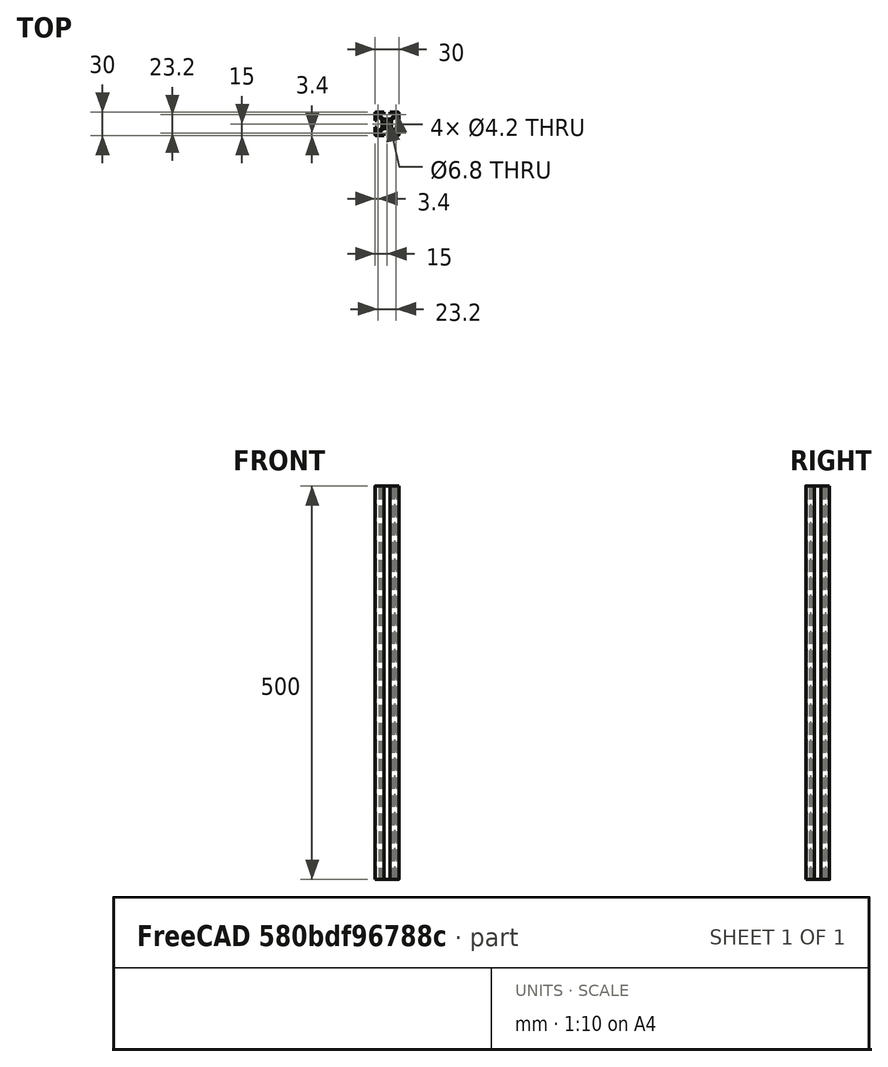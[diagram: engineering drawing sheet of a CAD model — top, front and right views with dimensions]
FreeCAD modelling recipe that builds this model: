
FCSTD DOCUMENT  (FreeCAD 0.19R24267 +99 (Git))
Label: misumi_profile_hfs_serie6_w8_30x30_Parametrique
License: All rights reserved
LicenseURL: http://en.wikipedia.org/wiki/All_rights_reserved
objects: Sketcher::SketchObject×1, Spreadsheet::Sheet×1, PartDesign::Pad×1, PartDesign::Body×1, App::Part×1
note: 4 computed .brp shape members not serialized (recipe doc carries the construction recipe); baked Part::Feature solids carry a one-line shape summary decoded from their .brp

FEATURE [Sketcher::SketchObject] Sketch  label="Profile"
  FullyConstrained = true
  MapMode = 5
  sketch-geometry (53):
    g0: LineSegment StartX=-6 StartY=-4.58579 StartZ=0 EndX=-6 EndY=4.58579 EndZ=0
    g1: LineSegment StartX=4.58579 StartY=6 StartZ=0 EndX=-4.58579 EndY=6 EndZ=0
    g2: LineSegment StartX=-6 StartY=4.58579 StartZ=0 EndX=-9.66421 EndY=8.25 EndZ=0
    g3: LineSegment StartX=-4.58579 StartY=6 StartZ=0 EndX=-8.25 EndY=9.66421 EndZ=0
    g4: LineSegment StartX=-9.66421 StartY=8.25 StartZ=0 EndX=-13 EndY=8.25 EndZ=0
    g5: LineSegment StartX=-13 StartY=8.25 StartZ=0 EndX=-13 EndY=4 EndZ=0
    g6: LineSegment StartX=-8.25 StartY=9.66421 StartZ=0 EndX=-8.25 EndY=13 EndZ=0
    g7: LineSegment StartX=-8.25 StartY=13 StartZ=0 EndX=-4 EndY=13 EndZ=0
    g8: LineSegment StartX=-13 StartY=4 StartZ=0 EndX=-15 EndY=4 EndZ=0
    g9: LineSegment StartX=-4 StartY=13 StartZ=0 EndX=-4 EndY=15 EndZ=0
    g10: LineSegment StartX=-4 StartY=15 StartZ=0 EndX=-14 EndY=15 EndZ=0
    g11: LineSegment StartX=-15 StartY=4 StartZ=0 EndX=-15 EndY=14 EndZ=0
    g12: ArcOfCircle CenterX=-14 CenterY=14 CenterZ=0 NormalX=0 NormalY=0 NormalZ=1 AngleXU=0 Radius=1 StartAngle=1.5708 EndAngle=3.14159
    g13: Circle CenterX=-11.6 CenterY=11.6 CenterZ=0 NormalX=0 NormalY=0 NormalZ=1 AngleXU=0 Radius=2.1
    g14: Circle CenterX=0 CenterY=0 CenterZ=0 NormalX=0 NormalY=0 NormalZ=1 AngleXU=0 Radius=3.4
    g15: LineSegment StartX=6 StartY=4.58579 StartZ=0 EndX=6 EndY=-4.58579 EndZ=0
    g16: LineSegment StartX=4.58579 StartY=6 StartZ=0 EndX=8.25 EndY=9.66421 EndZ=0
    g17: LineSegment StartX=8.25 StartY=9.66421 StartZ=0 EndX=8.25 EndY=13 EndZ=0
    g18: LineSegment StartX=8.25 StartY=13 StartZ=0 EndX=4 EndY=13 EndZ=0
    g19: LineSegment StartX=4 StartY=13 StartZ=0 EndX=4 EndY=15 EndZ=0
    g20: LineSegment StartX=6 StartY=4.58579 StartZ=0 EndX=9.66421 EndY=8.25 EndZ=0
    g21: LineSegment StartX=9.66421 StartY=8.25 StartZ=0 EndX=13 EndY=8.25 EndZ=0
    g22: LineSegment StartX=13 StartY=8.25 StartZ=0 EndX=13 EndY=4 EndZ=0
    g23: LineSegment StartX=13 StartY=4 StartZ=0 EndX=15 EndY=4 EndZ=0
    g24: LineSegment StartX=15 StartY=4 StartZ=0 EndX=15 EndY=14 EndZ=0
    g25: Circle CenterX=11.6 CenterY=11.6 CenterZ=0 NormalX=0 NormalY=0 NormalZ=1 AngleXU=0 Radius=2.1
    g26: LineSegment StartX=4 StartY=15 StartZ=0 EndX=14 EndY=15 EndZ=0
    g27: ArcOfCircle CenterX=14 CenterY=14 CenterZ=0 NormalX=0 NormalY=0 NormalZ=1 AngleXU=0 Radius=1 StartAngle=6.28319 EndAngle=7.85398
    g28: LineSegment StartX=6 StartY=-4.58579 StartZ=0 EndX=9.66421 EndY=-8.25 EndZ=0
    g29: LineSegment StartX=9.66421 StartY=-8.25 StartZ=0 EndX=13 EndY=-8.25 EndZ=0
    g30: LineSegment StartX=13 StartY=-8.25 StartZ=0 EndX=13 EndY=-4 EndZ=0
    g31: LineSegment StartX=13 StartY=-4 StartZ=0 EndX=15 EndY=-4 EndZ=0
    g32: LineSegment StartX=15 StartY=-4 StartZ=0 EndX=15 EndY=-14 EndZ=0
    g33: LineSegment StartX=14 StartY=-15 StartZ=0 EndX=4 EndY=-15 EndZ=0
    g34: LineSegment StartX=4 StartY=-15 StartZ=0 EndX=4 EndY=-13 EndZ=0
    g35: LineSegment StartX=4 StartY=-13 StartZ=0 EndX=8.25 EndY=-13 EndZ=0
    g36: LineSegment StartX=8.25 StartY=-13 StartZ=0 EndX=8.25 EndY=-9.66421 EndZ=0
    g37: LineSegment StartX=8.25 StartY=-9.66421 StartZ=0 EndX=4.58579 EndY=-6 EndZ=0
    g38: LineSegment StartX=4.58579 StartY=-6 StartZ=0 EndX=-4.58579 EndY=-6 EndZ=0
    g39: LineSegment StartX=-4.58579 StartY=-6 StartZ=0 EndX=-8.25 EndY=-9.66421 EndZ=0
    g40: LineSegment StartX=-8.25 StartY=-9.66421 StartZ=0 EndX=-8.25 EndY=-13 EndZ=0
    g41: LineSegment StartX=-8.25 StartY=-13 StartZ=0 EndX=-4 EndY=-13 EndZ=0
    g42: LineSegment StartX=-4 StartY=-13 StartZ=0 EndX=-4 EndY=-15 EndZ=0
    g43: LineSegment StartX=-4 StartY=-15 StartZ=0 EndX=-14 EndY=-15 EndZ=0
    g44: ArcOfCircle CenterX=14 CenterY=-14 CenterZ=0 NormalX=0 NormalY=0 NormalZ=1 AngleXU=0 Radius=1 StartAngle=4.71239 EndAngle=6.28319
    g45: LineSegment StartX=-6 StartY=-4.58579 StartZ=0 EndX=-9.66421 EndY=-8.25 EndZ=0
    g46: LineSegment StartX=-9.66421 StartY=-8.25 StartZ=0 EndX=-13 EndY=-8.25 EndZ=0
    g47: LineSegment StartX=-13 StartY=-8.25 StartZ=0 EndX=-13 EndY=-4 EndZ=0
    g48: LineSegment StartX=-13 StartY=-4 StartZ=0 EndX=-15 EndY=-4 EndZ=0
    g49: LineSegment StartX=-15 StartY=-4 StartZ=0 EndX=-15 EndY=-14 EndZ=0
    g50: ArcOfCircle CenterX=-14 CenterY=-14 CenterZ=0 NormalX=0 NormalY=0 NormalZ=1 AngleXU=0 Radius=1 StartAngle=3.14159 EndAngle=4.71239
    g51: Circle CenterX=-11.6 CenterY=-11.6 CenterZ=0 NormalX=0 NormalY=0 NormalZ=1 AngleXU=0 Radius=2.1
    g52: Circle CenterX=11.6 CenterY=-11.6 CenterZ=0 NormalX=0 NormalY=0 NormalZ=1 AngleXU=0 Radius=2.1
  constraints (124):
    c: DistanceX(g-1,g0) = -6
    c: Vertical(g0)
    c: Equal(g0,g1)
    c: Coincident(g0,g2)
    c: Angle(g2,g0) = 2.35619
    c: Coincident(g3,g1)
    c: Parallel(g2,g3)
    c: Equal(g3,g2)
    c: Coincident(g4,g2)
    c: Horizontal(g4)
    c: Coincident(g4,g5)
    c: Vertical(g5)
    c: Coincident(g6,g3)
    c: Vertical(g6)
    c: Equal(g4,g6)
    c: Coincident(g7,g6)
    c: Horizontal(g7)
    c: Equal(g7,g5)
    c: Coincident(g8,g5)
    c: Horizontal(g8)
    c: Coincident(g9,g7)
    c: Vertical(g9)
    c: DistanceX(g-1,g7) = -4
    c: DistanceY(g9) = 2
    c: Coincident(g10,g9)
    c: Horizontal(g10)
    c: Coincident(g11,g8)
    c: Vertical(g11)
    c: Equal(g10,g11)
    c: DistanceY(g-1,g10) = 15
    c: Coincident(g12,g10)
    c: Coincident(g12,g11)
    c: Radius(g12) = 1
    c: Tangent(g12,g11)
    c: Equal(g8,g9)
    c: Distance(g1,g0) = 2
    c: DistanceX(g-1,g3) = -8.25
    c: Radius(g13) = 2.1
    c: DistanceY(g-1,g13) = 11.6
    c: DistanceX(g-1,g13) = -11.6
    c: Coincident(g14,g-1)
    c: Radius(g14) = 3.4
    c: DistanceY(g-1,g1) = 6
    c: DistanceY(g-1,g5) = 4
    c: Symmetric(g15,g0,g-2)
    c: Symmetric(g0,g15,g-2)
    c: Coincident(g16,g1)
    c: Symmetric(g1,g1,g-2)
    c: Symmetric(g16,g3,g-2)
    c: Coincident(g17,g16)
    c: Symmetric(g17,g6,g-2)
    c: Coincident(g18,g17)
    c: Symmetric(g18,g7,g-2)
    c: Coincident(g19,g18)
    c: Symmetric(g19,g9,g-2)
    c: Coincident(g20,g21)
    c: Coincident(g21,g22)
    c: Coincident(g22,g23)
    c: Coincident(g23,g24)
    c: Coincident(g20,g15)
    c: Symmetric(g20,g2,g-2)
    c: Symmetric(g21,g4,g-2)
    c: Symmetric(g22,g5,g-2)
    c: Symmetric(g23,g8,g-2)
    c: Symmetric(g24,g11,g-2)
    c: Symmetric(g25,g13,g-2)
    c: Equal(g25,g13)
    c: Coincident(g26,g19)
    c: Symmetric(g26,g10,g-2)
    c: Tangent(g27,g26) = 1.5708
    c: Radius(g27) = 1
    c: Coincident(g27,g24)
    c: Coincident(g28,g29)
    c: Coincident(g29,g30)
    c: Coincident(g30,g31)
    c: Coincident(g31,g32)
    c: Coincident(g28,g15)
    c: Symmetric(g28,g20,g-1)
    c: Symmetric(g29,g21,g-1)
    c: Symmetric(g30,g22,g-1)
    c: Symmetric(g31,g23,g-1)
    c: Symmetric(g32,g24,g-1)
    c: Coincident(g33,g34)
    c: Coincident(g34,g35)
    c: Coincident(g35,g36)
    c: Coincident(g36,g37)
    c: Coincident(g37,g38)
    c: Coincident(g38,g39)
    c: Coincident(g39,g40)
    c: Coincident(g40,g41)
    c: Coincident(g41,g42)
    c: Coincident(g42,g43)
    c: Symmetric(g42,g9,g-1)
    c: Symmetric(g41,g7,g-1)
    c: Symmetric(g40,g6,g-1)
    c: Symmetric(g39,g3,g-1)
    c: Symmetric(g38,g1,g-1)
    c: Symmetric(g37,g1,g-1)
    c: Symmetric(g36,g16,g-1)
    c: Symmetric(g35,g17,g-1)
    c: Symmetric(g34,g18,g-1)
    c: Symmetric(g33,g19,g-1)
    c: Symmetric(g33,g26,g-1)
    c: Radius(g44) = 1
    c: Coincident(g44,g33)
    c: Coincident(g44,g32)
    c: Symmetric(g43,g10,g-1)
    c: Coincident(g45,g46)
    c: Coincident(g46,g47)
    c: Coincident(g47,g48)
    c: Coincident(g48,g49)
    c: Coincident(g0,g45)
    c: Symmetric(g45,g2,g-1)
    c: Symmetric(g46,g4,g-1)
    c: Symmetric(g47,g5,g-1)
    c: Symmetric(g48,g8,g-1)
    c: Symmetric(g49,g11,g-1)
    c: Coincident(g50,g49)
    c: Coincident(g50,g43)
    c: Tangent(g50,g49)
    c: Symmetric(g51,g13,g-1)
    c: Equal(g51,g13)
    c: Symmetric(g52,g51,g-2)
    c: Equal(g52,g51)
FEATURE [Spreadsheet::Sheet] Spreadsheet  label="perfil_misumi_hfs30x30w009"
  cells = A1=Longueur; B1(Longeur)=500
FEATURE [PartDesign::Pad] Pad
  Direction = (1,1,1)
  Length = 500
  Length2 = 100
  Profile = -> Sketch
  Type = 0
  expr: Length = <<perfil_misumi_hfs30x30w009>>.Longeur
FEATURE [PartDesign::Body] Body
  Group = -> [Sketch,Pad]
  Origin = -> Origin021
  Tip = -> Pad
FEATURE [App::Part] Part  label="perfil_misumi_hfs30x30w009 :500mm"
  Group = -> [Spreadsheet,Body]
  Origin = -> Origin
  expr: Label = <<perfil_misumi_hfs30x30w009 :%s>> % +<<perfil_misumi_hfs30x30w009>>.Longeur + <<mm>>
